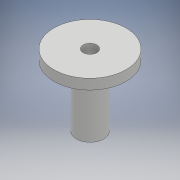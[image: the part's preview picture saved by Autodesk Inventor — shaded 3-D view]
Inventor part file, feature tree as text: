
AUTODESK INVENTOR PART (.ipt)
format: ipt  version: 2017 (Build 210142000, 142)  size: 107,520 bytes
history: native  units: mm
features: sketch x4, extrude x2, hole x2
ambient origin geometry x8: Origin, YZ Plane, XZ Plane, XY Plane, X Axis, Y Axis, Z Axis, Center Point
bodies: Solid1 (feature_tree)
feature tree (8):
  extrude  "Extrusion1"  Depth=56.896mm TaperAngle=0.0deg
  hole  "Hole1"  [1 undecoded]
  extrude  "Extrusion2"  [1 undecoded]
  hole  "Hole2"  [1 undecoded]
  sketch  "Sketch1"  dims[d0=25.4mm d2=56.896mm d3=0.0mm]
  sketch  "Sketch2"  dims[d4=12.7mm]
  sketch  "Sketch5"  dims[d5=12.7mm d6=6.0mm d7=4.0mm d8=2.0mm d9=90.0deg d10=8.0mm d11=20.594885mm d12=67.183mm]
  sketch  "Sketch6"  dims[d13=9.525mm d14=0.0mm d15=12.7mm d16=6.0mm d17=4.0mm d18=2.0mm d19=90.0deg d20=8.0mm d21=20.594885mm]
note: 3 required parameter values undecoded (feature->parameter linkage not recoverable at this tier; creation-order binding heuristic only, values carry confidence <= 0.55)
